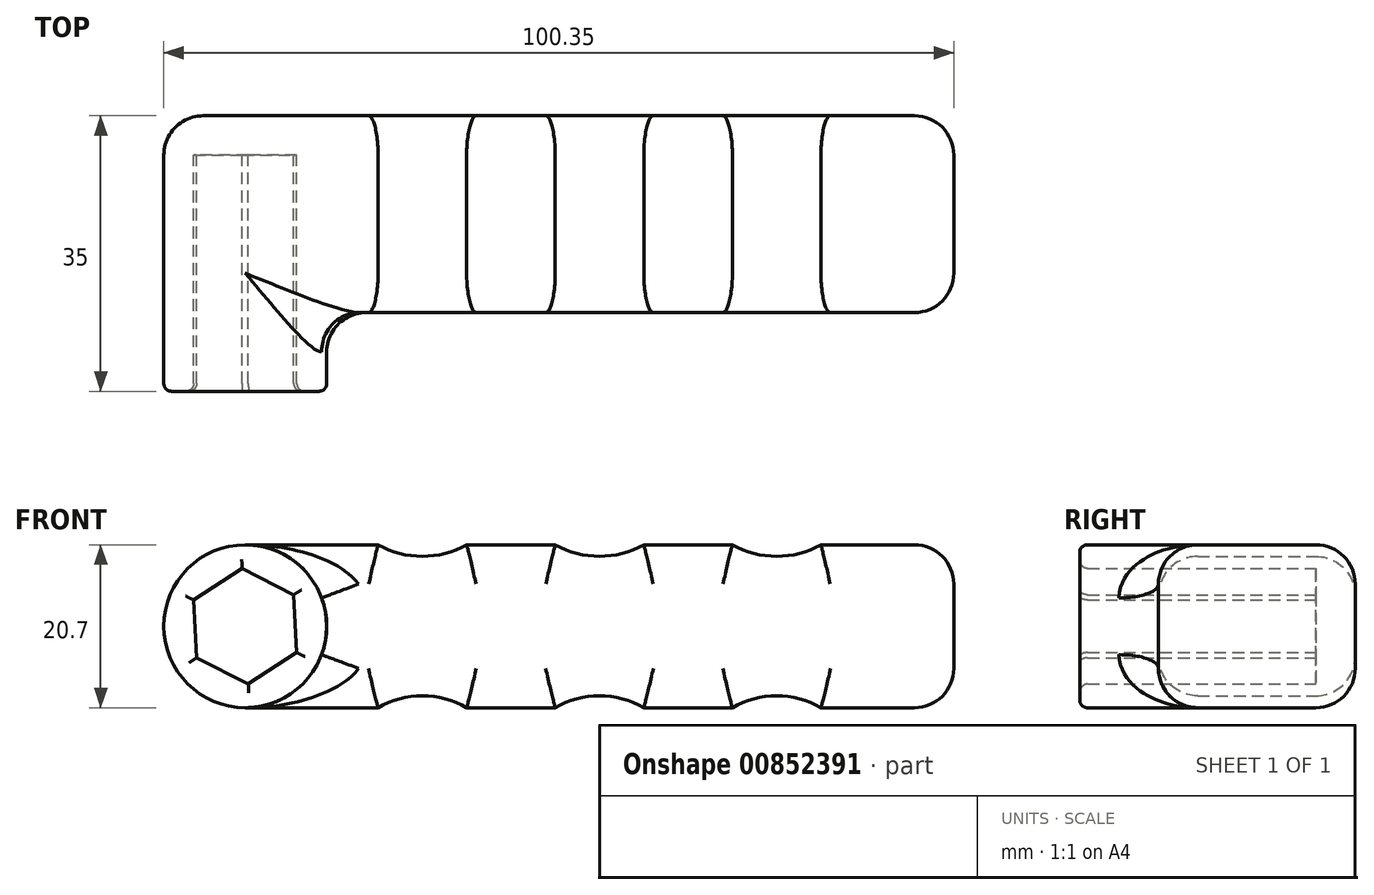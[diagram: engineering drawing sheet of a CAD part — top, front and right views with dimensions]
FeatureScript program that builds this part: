
annotation { "Feature Type Name" : "Feature", "Feature Type Description" : "" }
export const myFeature = defineFeature(function(context is Context, id is Id, definition is map)
    precondition{}
    {
        {
            var Q0;
            Q0=qCreatedBy(makeId("Front.planeOp"),FACE);
            var sketch = newSketch(context, id + "F0", { "sketchPlane" : qUnion([Q0])});
            skCircle(sketch, "E0.cCircle", {"center": v(-99.8, 40.1) * mm, "radius": 7.35 * mm, "construction": true});
            skLineSegment(sketch, "E0.0", {"start": v(-99.41, 32.76) * mm, "end": v(-105.96, 36.1) * mm});
            skLineSegment(sketch, "E0.1", {"start": v(-105.96, 36.1) * mm, "end": v(-106.35, 43.44) * mm});
            skLineSegment(sketch, "E0.2", {"start": v(-106.35, 43.44) * mm, "end": v(-100.18, 47.44) * mm});
            skLineSegment(sketch, "E0.3", {"start": v(-100.18, 47.44) * mm, "end": v(-93.63, 44.1) * mm});
            skLineSegment(sketch, "E0.4", {"start": v(-93.63, 44.1) * mm, "end": v(-93.25, 36.76) * mm});
            skLineSegment(sketch, "E0.5", {"start": v(-93.25, 36.76) * mm, "end": v(-99.41, 32.76) * mm});
            skCircle(sketch, "E1.0", {"center": v(-99.8, 40.1) * mm, "radius": 10.35 * mm});
            skPoint(sketch, "E2", {"position": v(-99.8, 50.45) * mm});
            skPoint(sketch, "E3", {"position": v(-99.8, 29.75) * mm});
            skLineSegment(sketch, "E4.bottom", {"start": v(-99.8, 50.45) * mm, "end": v(-88.55, 50.45) * mm});
            skLineSegment(sketch, "E4.top", {"start": v(-99.8, 29.75) * mm, "end": v(-88.55, 29.75) * mm});
            skLineSegment(sketch, "E4.right", {"start": v(-9.8, 50.45) * mm, "end": v(-9.8, 29.75) * mm});
            skLineSegment(sketch, "E5", {"start": v(-88.55, 29.75) * mm, "end": v(-82.92, 29.75) * mm});
            skLineSegment(sketch, "E6", {"start": v(-66.05, 29.75) * mm, "end": v(-60.42, 29.75) * mm});
            skLineSegment(sketch, "E7", {"start": v(-43.55, 29.75) * mm, "end": v(-37.92, 29.75) * mm});
            skLineSegment(sketch, "E8", {"start": v(-21.05, 29.75) * mm, "end": v(-9.8, 29.75) * mm});
            skLineSegment(sketch, "E9", {"start": v(-88.55, 50.45) * mm, "end": v(-82.92, 50.45) * mm});
            skLineSegment(sketch, "E10", {"start": v(-66.05, 50.45) * mm, "end": v(-60.42, 50.45) * mm});
            skLineSegment(sketch, "E11", {"start": v(-43.55, 50.45) * mm, "end": v(-37.92, 50.45) * mm});
            skLineSegment(sketch, "E12", {"start": v(-21.05, 50.45) * mm, "end": v(-9.8, 50.45) * mm});
            skArc(sketch, "E13", {"start": v(-82.92, 29.75) * mm, "mid": v(-77.3, 31.27) * mm, "end": v(-71.67, 29.75) * mm});
            skArc(sketch, "E14", {"start": v(-60.42, 29.75) * mm, "mid": v(-54.8, 31.27) * mm, "end": v(-49.17, 29.75) * mm});
            skArc(sketch, "E15", {"start": v(-37.92, 29.75) * mm, "mid": v(-32.3, 31.27) * mm, "end": v(-26.67, 29.75) * mm});
            skArc(sketch, "E16", {"start": v(-26.67, 50.45) * mm, "mid": v(-32.3, 48.98) * mm, "end": v(-37.92, 50.45) * mm});
            skArc(sketch, "E17", {"start": v(-49.17, 50.45) * mm, "mid": v(-54.8, 48.98) * mm, "end": v(-60.42, 50.45) * mm});
            skArc(sketch, "E18", {"start": v(-71.67, 50.45) * mm, "mid": v(-77.3, 48.98) * mm, "end": v(-82.92, 50.45) * mm});
            skLineSegment(sketch, "E19", {"start": v(-71.67, 29.75) * mm, "end": v(-66.05, 29.75) * mm});
            skLineSegment(sketch, "E20", {"start": v(-49.17, 29.75) * mm, "end": v(-43.55, 29.75) * mm});
            skLineSegment(sketch, "E21", {"start": v(-26.67, 29.75) * mm, "end": v(-21.05, 29.75) * mm});
            skLineSegment(sketch, "E22", {"start": v(-26.67, 50.45) * mm, "end": v(-21.05, 50.45) * mm});
            skLineSegment(sketch, "E23", {"start": v(-49.17, 50.45) * mm, "end": v(-43.55, 50.45) * mm});
            skLineSegment(sketch, "E24", {"start": v(-71.67, 50.45) * mm, "end": v(-66.05, 50.45) * mm});
            skSolve(sketch);
        }
        {
            var Q0;
            {var subQ1=sQuery(id+"F0.wireOp",EDGE,"E4.bottom");Q0=makeQuery(id+"F0.imprint","IMPRINT",FACE,{"disambiguationData":[TD([[makeQuery(id+"F0.imprint","IMPRINT",EDGE,{"derivedFrom":subQ1}),-1.0]])]});}
            extrude(context, id + "F1", {"entities" : qUnion([Q0]), "depth" : 25 * mm, "offsetDistance" : 25 * mm});
        }
        {
            var Q0;
            Q0=makeQuery(id+"F0.imprint","IMPRINT",FACE,{"disambiguationData":[TD([[makeQuery(id+"F0.imprint","IMPRINT",EDGE,{"derivedFrom":sQuery(id+"F0.wireOp",EDGE,"E0.0")}),1.0]])]});
            extrude(context, id + "F2", {"entities" : qUnion([Q0]), "operationType" : NewBodyOperationType.ADD, "depth" : 35 * mm, "offsetDistance" : 25 * mm});
        }
        {
            var Q0;
            Q0=makeQuery(id+"F0.imprint","IMPRINT",FACE,{"disambiguationData":[TD([[makeQuery(id+"F0.imprint","IMPRINT",EDGE,{"derivedFrom":sQuery(id+"F0.wireOp",EDGE,"E0.0")}),-1.0]])]});
            extrude(context, id + "F3", {"entities" : qUnion([Q0]), "operationType" : NewBodyOperationType.ADD, "depth" : 5 * mm, "offsetDistance" : 25 * mm});
        }
        {
            var Q0;
            Q0=makeQuery(id+"F1.opExtrude","CAP_FACE",FACE,{"disambiguationData":[OSD([sQuery(id+"F0.wireOp",EDGE,"E1.0"),sQuery(id+"F0.wireOp",EDGE,"E4.bottom"),sQuery(id+"F0.wireOp",EDGE,"E4.top"),sQuery(id+"F0.wireOp",EDGE,"E4.right"),sQuery(id+"F0.wireOp",EDGE,"E5"),sQuery(id+"F0.wireOp",EDGE,"E6"),sQuery(id+"F0.wireOp",EDGE,"E7"),sQuery(id+"F0.wireOp",EDGE,"E8"),sQuery(id+"F0.wireOp",EDGE,"E9"),sQuery(id+"F0.wireOp",EDGE,"E10"),sQuery(id+"F0.wireOp",EDGE,"E11"),sQuery(id+"F0.wireOp",EDGE,"E12"),sQuery(id+"F0.wireOp",EDGE,"E13"),sQuery(id+"F0.wireOp",EDGE,"E14"),sQuery(id+"F0.wireOp",EDGE,"E15"),sQuery(id+"F0.wireOp",EDGE,"E16"),sQuery(id+"F0.wireOp",EDGE,"E17"),sQuery(id+"F0.wireOp",EDGE,"E18"),sQuery(id+"F0.wireOp",EDGE,"E19"),sQuery(id+"F0.wireOp",EDGE,"E20"),sQuery(id+"F0.wireOp",EDGE,"E21"),sQuery(id+"F0.wireOp",EDGE,"E22"),sQuery(id+"F0.wireOp",EDGE,"E23"),sQuery(id+"F0.wireOp",EDGE,"E24")])],"isStart":false});
            var Q1;
            {var subQ0=sQuery(id+"F0.wireOp",EDGE,"E0.5");var subQ1=sQuery(id+"F0.wireOp",EDGE,"E0.4");var subQ2=sQuery(id+"F0.wireOp",EDGE,"E0.3");var subQ3=sQuery(id+"F0.wireOp",EDGE,"E0.2");var subQ4=sQuery(id+"F0.wireOp",EDGE,"E0.1");var subQ5=sQuery(id+"F0.wireOp",EDGE,"E0.0");var subQ6=sQuery(id+"F0.wireOp",EDGE,"E1.0");Q1=makeQuery(id+"F3.boolean.opBoolean","MERGE",FACE,{"derivedFrom":[makeQuery(id+"F2.boolean.opBoolean","MERGE",FACE,{"derivedFrom":[makeQuery(id+"F1.opExtrude","CAP_FACE",FACE,{"disambiguationData":[OSD([subQ6,sQuery(id+"F0.wireOp",EDGE,"E4.bottom"),sQuery(id+"F0.wireOp",EDGE,"E4.top"),sQuery(id+"F0.wireOp",EDGE,"E4.right"),sQuery(id+"F0.wireOp",EDGE,"E5"),sQuery(id+"F0.wireOp",EDGE,"E6"),sQuery(id+"F0.wireOp",EDGE,"E7"),sQuery(id+"F0.wireOp",EDGE,"E8"),sQuery(id+"F0.wireOp",EDGE,"E9"),sQuery(id+"F0.wireOp",EDGE,"E10"),sQuery(id+"F0.wireOp",EDGE,"E11"),sQuery(id+"F0.wireOp",EDGE,"E12"),sQuery(id+"F0.wireOp",EDGE,"E13"),sQuery(id+"F0.wireOp",EDGE,"E14"),sQuery(id+"F0.wireOp",EDGE,"E15"),sQuery(id+"F0.wireOp",EDGE,"E16"),sQuery(id+"F0.wireOp",EDGE,"E17"),sQuery(id+"F0.wireOp",EDGE,"E18"),sQuery(id+"F0.wireOp",EDGE,"E19"),sQuery(id+"F0.wireOp",EDGE,"E20"),sQuery(id+"F0.wireOp",EDGE,"E21"),sQuery(id+"F0.wireOp",EDGE,"E22"),sQuery(id+"F0.wireOp",EDGE,"E23"),sQuery(id+"F0.wireOp",EDGE,"E24")])],"isStart":true}),makeQuery(id+"F2.opExtrude","CAP_FACE",FACE,{"disambiguationData":[OSD([subQ5,subQ4,subQ3,subQ2,subQ1,subQ0,subQ6])],"isStart":true})]}),makeQuery(id+"F3.opExtrude","CAP_FACE",FACE,{"disambiguationData":[OSD([subQ5,subQ4,subQ3,subQ2,subQ1,subQ0])],"isStart":true})]});}
            var Q2;
            Q2=makeQuery(id+"F1.opExtrude","SWEPT_EDGE",EDGE,{"disambiguationData":[OSD([sQuery(id+"F0.wireOp",EDGE,"E4.right"),sQuery(id+"F0.wireOp",EDGE,"E8")])]});
            var Q3;
            Q3=makeQuery(id+"F1.opExtrude","SWEPT_EDGE",EDGE,{"disambiguationData":[OSD([sQuery(id+"F0.wireOp",EDGE,"E4.right"),sQuery(id+"F0.wireOp",EDGE,"E12")])]});
            fillet(context, id + "F4", {"entities" : qUnion([Q0, Q1, Q2, Q3]), "radius" : 5 * mm, "tangentPropagation" : true, "allowEdgeOverflow" : false});
        }
        {
            var Q0;
            Q0=makeQuery(id+"F2.opExtrude","CAP_FACE",FACE,{"disambiguationData":[OSD([sQuery(id+"F0.wireOp",EDGE,"E0.0"),sQuery(id+"F0.wireOp",EDGE,"E0.1"),sQuery(id+"F0.wireOp",EDGE,"E0.2"),sQuery(id+"F0.wireOp",EDGE,"E0.3"),sQuery(id+"F0.wireOp",EDGE,"E0.4"),sQuery(id+"F0.wireOp",EDGE,"E0.5"),sQuery(id+"F0.wireOp",EDGE,"E1.0")])],"isStart":false});
            fillet(context, id + "F5", {"entities" : qUnion([Q0]), "radius" : 1 * mm, "tangentPropagation" : true, "allowEdgeOverflow" : false});
        }
    });
